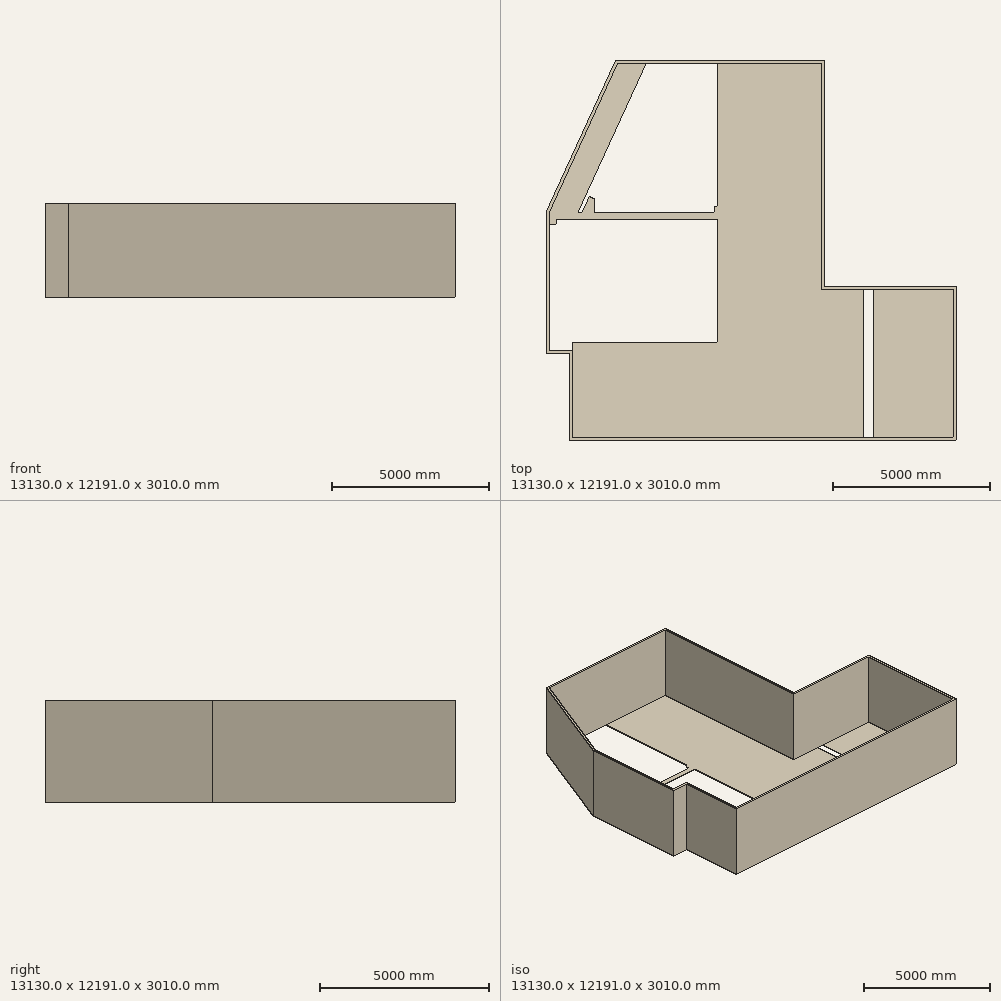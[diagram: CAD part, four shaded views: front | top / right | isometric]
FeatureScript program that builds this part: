
annotation { "Feature Type Name" : "Feature", "Feature Type Description" : "" }
export const myFeature = defineFeature(function(context is Context, id is Id, definition is map)
    precondition{}
    {
        {
            var Q0;
            Q0=qCreatedBy(makeId("Top.planeOp"),FACE);
            var sketch = newSketch(context, id + "F0", { "sketchPlane" : qUnion([Q0])});
            skLineSegment(sketch, "E0.bottom", {"start": v(0, 0) * mm, "end": v(20000, 0) * mm, "construction": true});
            skLineSegment(sketch, "E0.top", {"start": v(0, 22000) * mm, "end": v(20000, 22000) * mm, "construction": true});
            skLineSegment(sketch, "E0.left", {"start": v(0, 0) * mm, "end": v(0, 22000) * mm, "construction": true});
            skLineSegment(sketch, "E0.right", {"start": v(20000, 0) * mm, "end": v(20000, 22000) * mm, "construction": true});
            skLineSegment(sketch, "E1.bottom", {"start": v(0, 0) * mm, "end": v(400, 0) * mm, "construction": true});
            skLineSegment(sketch, "E1.top", {"start": v(0, 400) * mm, "end": v(400, 400) * mm, "construction": true});
            skLineSegment(sketch, "E1.left", {"start": v(0, 0) * mm, "end": v(0, 400) * mm, "construction": true});
            skLineSegment(sketch, "E1.right", {"start": v(400, 0) * mm, "end": v(400, 400) * mm, "construction": true});
            skPoint(sketch, "E2", {"position": v(400, 400) * mm});
            skLineSegment(sketch, "E3", {"start": v(400, -1815.56) * mm, "end": v(13100, -1815.56) * mm, "construction": true});
            skPoint(sketch, "E3.startSnap0", {"position": v(400, 200) * mm});
            skPoint(sketch, "E4", {"position": v(6750, -1815.56) * mm});
            skSolve(sketch);
        }
        {
            var Q0;
            Q0=qCreatedBy(makeId("Top.planeOp"),FACE);
            var sketch = newSketch(context, id + "F1", { "sketchPlane" : qUnion([Q0])});
            skLineSegment(sketch, "E5.bottom", {"start": v(400, 400) * mm, "end": v(5050, 400) * mm});
            skLineSegment(sketch, "E5.top", {"start": v(400, 3200) * mm, "end": v(5050, 3200) * mm});
            skLineSegment(sketch, "E5.left", {"start": v(400, 400) * mm, "end": v(400, 3200) * mm});
            skLineSegment(sketch, "E5.right", {"start": v(5050, 400) * mm, "end": v(5050, 3200) * mm});
            skLineSegment(sketch, "E6.bottom", {"start": v(-330, 3440.5) * mm, "end": v(5050, 3440.5) * mm});
            skLineSegment(sketch, "E6.top", {"start": v(-330, 7380.5) * mm, "end": v(5050, 7380.5) * mm});
            skLineSegment(sketch, "E6.left", {"start": v(-330, 3440.5) * mm, "end": v(-330, 7380.5) * mm});
            skLineSegment(sketch, "E6.right", {"start": v(5050, 3440.5) * mm, "end": v(5050, 7380.5) * mm});
            skLineSegment(sketch, "E7.bottom", {"start": v(8384.88, 7120) * mm, "end": v(6584.88, 7120) * mm});
            skLineSegment(sketch, "E7.top", {"start": v(8384.88, 4070) * mm, "end": v(6584.88, 4070) * mm});
            skLineSegment(sketch, "E7.left", {"start": v(8384.88, 7120) * mm, "end": v(8384.88, 4070) * mm});
            skLineSegment(sketch, "E7.right", {"start": v(6584.88, 7120) * mm, "end": v(6584.88, 4070) * mm});
            skLineSegment(sketch, "E8.bottom", {"start": v(12600, 5151.66) * mm, "end": v(10030, 5151.66) * mm});
            skLineSegment(sketch, "E8.top", {"start": v(12600, 400) * mm, "end": v(10030, 400) * mm});
            skLineSegment(sketch, "E8.left", {"start": v(12600, 5151.66) * mm, "end": v(12600, 400) * mm});
            skLineSegment(sketch, "E8.right", {"start": v(10030, 5151.66) * mm, "end": v(10030, 400) * mm});
            skLineSegment(sketch, "E9.bottom", {"start": v(5347.44, 7120) * mm, "end": v(6287.44, 7120) * mm});
            skLineSegment(sketch, "E9.top", {"start": v(5347.44, 400) * mm, "end": v(6287.44, 400) * mm});
            skLineSegment(sketch, "E9.left", {"start": v(5347.44, 7120) * mm, "end": v(5347.44, 400) * mm});
            skLineSegment(sketch, "E9.right", {"start": v(6287.44, 7120) * mm, "end": v(6287.44, 400) * mm});
            skLineSegment(sketch, "E10.bottom", {"start": v(6287.44, 400) * mm, "end": v(9732.56, 400) * mm});
            skLineSegment(sketch, "E10.top", {"start": v(6287.44, 2060) * mm, "end": v(9732.56, 2060) * mm});
            skLineSegment(sketch, "E10.left", {"start": v(6287.44, 400) * mm, "end": v(6287.44, 2060) * mm});
            skLineSegment(sketch, "E10.right", {"start": v(9732.56, 400) * mm, "end": v(9732.56, 2060) * mm});
            skLineSegment(sketch, "E11.bottom", {"start": v(8384.88, 2166.08) * mm, "end": v(6584.88, 2166.08) * mm});
            skLineSegment(sketch, "E11.top", {"start": v(8384.88, 4016.08) * mm, "end": v(6584.88, 4016.08) * mm});
            skLineSegment(sketch, "E11.left", {"start": v(8384.88, 2166.08) * mm, "end": v(8384.88, 4016.08) * mm});
            skLineSegment(sketch, "E11.right", {"start": v(6584.88, 2166.08) * mm, "end": v(6584.88, 4016.08) * mm});
            skLineSegment(sketch, "E12.bottom", {"start": v(9732.56, 2151.66) * mm, "end": v(8782.56, 2151.66) * mm});
            skLineSegment(sketch, "E12.top", {"start": v(9732.56, 5151.66) * mm, "end": v(8782.56, 5151.66) * mm});
            skLineSegment(sketch, "E12.left", {"start": v(9732.56, 2060) * mm, "end": v(9732.56, 5151.66) * mm});
            skLineSegment(sketch, "E12.right", {"start": v(8782.56, 2151.66) * mm, "end": v(8782.56, 5151.66) * mm});
            skLineSegment(sketch, "E13", {"start": v(-330, 7621.02) * mm, "end": v(1855.04, 12391.02) * mm});
            skLineSegment(sketch, "E14", {"start": v(1855.04, 12391.02) * mm, "end": v(5050, 12391.02) * mm});
            skLineSegment(sketch, "E15", {"start": v(5050, 12391.02) * mm, "end": v(5050, 7621.02) * mm});
            skLineSegment(sketch, "E16", {"start": v(5050, 7621.02) * mm, "end": v(-330, 7621.02) * mm});
            skLineSegment(sketch, "E17", {"start": v(587.33, 7621.02) * mm, "end": v(2772.37, 12391.02) * mm});
            skLineSegment(sketch, "E18.bottom", {"start": v(5347.44, 12391.02) * mm, "end": v(8384.88, 12391.02) * mm});
            skLineSegment(sketch, "E18.top", {"start": v(5347.44, 8631.02) * mm, "end": v(8384.88, 8631.02) * mm});
            skLineSegment(sketch, "E18.left", {"start": v(5347.44, 8631.02) * mm, "end": v(5347.44, 12391.02) * mm});
            skLineSegment(sketch, "E18.right", {"start": v(8384.88, 8631.02) * mm, "end": v(8384.88, 12391.02) * mm});
            skLineSegment(sketch, "E19", {"start": v(10030, 951.66) * mm, "end": v(12600, 951.66) * mm, "construction": true});
            skPoint(sketch, "E20", {"position": v(-330, 5410.5) * mm});
            skLineSegment(sketch, "E21", {"start": v(-6623.02, 7621.02) * mm, "end": v(-6623.02, 3200) * mm, "construction": true});
            skPoint(sketch, "E22", {"position": v(-6623.02, 5410.5) * mm});
            skPoint(sketch, "E23", {"position": v(5817.44, -1044.03) * mm});
            skPoint(sketch, "E24", {"position": v(5817.44, 400) * mm});
            skLineSegment(sketch, "E25.bottom", {"start": v(-110, 7380.5) * mm, "end": v(-330, 7380.5) * mm});
            skLineSegment(sketch, "E25.top", {"start": v(-110, 7240.5) * mm, "end": v(-330, 7240.5) * mm});
            skLineSegment(sketch, "E25.left", {"start": v(-110, 7380.5) * mm, "end": v(-110, 7240.5) * mm});
            skLineSegment(sketch, "E25.right", {"start": v(-330, 7380.5) * mm, "end": v(-330, 7240.5) * mm});
            skLineSegment(sketch, "E26", {"start": v(1120, 7621.02) * mm, "end": v(1120, 8039.5) * mm});
            skLineSegment(sketch, "E27", {"start": v(1120, 8039.5) * mm, "end": v(838.16, 8168.6) * mm});
            skLineSegment(sketch, "E28.bottom", {"start": v(5050, 7621.02) * mm, "end": v(4950, 7621.02) * mm});
            skLineSegment(sketch, "E28.top", {"start": v(5050, 7801.02) * mm, "end": v(4950, 7801.02) * mm});
            skLineSegment(sketch, "E28.left", {"start": v(5050, 7621.02) * mm, "end": v(5050, 7801.02) * mm});
            skLineSegment(sketch, "E28.right", {"start": v(4950, 7621.02) * mm, "end": v(4950, 7801.02) * mm});
            skLineSegment(sketch, "E29.bottom", {"start": v(12600, 5151.66) * mm, "end": v(12618.37, 5151.66) * mm});
            skLineSegment(sketch, "E29.top", {"start": v(12600, 4874.4) * mm, "end": v(12618.37, 4874.4) * mm});
            skLineSegment(sketch, "E29.left", {"start": v(12618.37, 5151.66) * mm, "end": v(12618.37, 4874.4) * mm});
            skLineSegment(sketch, "E29.right", {"start": v(12600, 5151.66) * mm, "end": v(12600, 4874.4) * mm});
            skLineSegment(sketch, "E30", {"start": v(717.56, 7621.02) * mm, "end": v(2902.6, 12391.02) * mm});
            skLineSegment(sketch, "E31", {"start": v(-330, 7621.02) * mm, "end": v(-330, 7380.5) * mm});
            skLineSegment(sketch, "E32", {"start": v(400, 3200) * mm, "end": v(400, 3440.5) * mm});
            skLineSegment(sketch, "E33", {"start": v(5050, 400) * mm, "end": v(5347.44, 400) * mm});
            skLineSegment(sketch, "E34", {"start": v(9732.56, 400) * mm, "end": v(10030, 400) * mm});
            skLineSegment(sketch, "E35", {"start": v(10030, 5151.66) * mm, "end": v(9732.56, 5151.66) * mm});
            skLineSegment(sketch, "E36", {"start": v(8782.56, 5151.66) * mm, "end": v(8384.88, 5151.66) * mm});
            skLineSegment(sketch, "E37", {"start": v(8384.88, 7120) * mm, "end": v(8384.88, 8631.02) * mm});
            skLineSegment(sketch, "E38", {"start": v(5050, 12391.02) * mm, "end": v(5347.44, 12391.02) * mm});
            skLineSegment(sketch, "E39", {"start": v(6584.88, 118.85) * mm, "end": v(5050, 118.85) * mm, "construction": true});
            skPoint(sketch, "E40", {"position": v(5817.44, 118.85) * mm});
            skLineSegment(sketch, "E41", {"start": v(5347.44, -349.5) * mm, "end": v(6287.44, -349.5) * mm, "construction": true});
            skPoint(sketch, "E42", {"position": v(5817.44, -349.5) * mm});
            skLineSegment(sketch, "E43", {"start": v(10030, -137.4) * mm, "end": v(8485.12, -137.4) * mm, "construction": true});
            skPoint(sketch, "E44", {"position": v(9257.56, 5151.66) * mm});
            skPoint(sketch, "E45", {"position": v(11591.26, 5335.33) * mm});
            skPoint(sketch, "E46", {"position": v(9257.56, -137.4) * mm});
            skPoint(sketch, "E47", {"position": v(9257.56, -547.39) * mm});
            skLineSegment(sketch, "E48", {"start": v(6287.44, -581.63) * mm, "end": v(6584.88, -581.63) * mm, "construction": true});
            skLineSegment(sketch, "E49", {"start": v(10030, -570.86) * mm, "end": v(9732.56, -570.86) * mm, "construction": true});
            skLineSegment(sketch, "E50", {"start": v(2902.6, 13575.57) * mm, "end": v(8384.88, 13575.57) * mm, "construction": true});
            skLineSegment(sketch, "E51", {"start": v(5050, 12932.31) * mm, "end": v(5347.44, 12932.31) * mm, "construction": true});
            skLineSegment(sketch, "E52", {"start": v(8802.5, 7120) * mm, "end": v(8802.5, 8631.02) * mm, "construction": true});
            skLineSegment(sketch, "E53", {"start": v(13053.8, 4070) * mm, "end": v(13053.8, 8631.02) * mm, "construction": true});
            skSolve(sketch);
        }
        {
            var Q0;
            Q0=qCreatedBy(makeId("Top.planeOp"),FACE);
            var sketch = newSketch(context, id + "F2", { "sketchPlane" : qUnion([Q0])});
            skPoint(sketch, "E54", {"position": v(400, 400) * mm});
            skPoint(sketch, "E55", {"position": v(-330, 3440.5) * mm});
            skPoint(sketch, "E56", {"position": v(-330, 7621.02) * mm});
            skPoint(sketch, "E57", {"position": v(1855.04, 12391.02) * mm});
            skPoint(sketch, "E58", {"position": v(8384.88, 12391.02) * mm});
            skPoint(sketch, "E59", {"position": v(8782.56, 5151.66) * mm});
            skPoint(sketch, "E60", {"position": v(12600, 5151.66) * mm});
            skPoint(sketch, "E61", {"position": v(12600, 400) * mm});
            skLineSegment(sketch, "E62", {"start": v(1855.04, 12391.02) * mm, "end": v(8384.88, 12391.02) * mm});
            skLineSegment(sketch, "E63", {"start": v(8384.88, 12391.02) * mm, "end": v(8384.88, 5151.66) * mm});
            skLineSegment(sketch, "E64", {"start": v(8384.88, 5151.66) * mm, "end": v(12600, 5151.66) * mm});
            skLineSegment(sketch, "E65", {"start": v(12600, 5151.66) * mm, "end": v(12600, 400) * mm});
            skLineSegment(sketch, "E66", {"start": v(12600, 400) * mm, "end": v(400, 400) * mm});
            skLineSegment(sketch, "E67", {"start": v(400, 400) * mm, "end": v(400, 3200) * mm});
            skLineSegment(sketch, "E68", {"start": v(400, 3200) * mm, "end": v(-330, 3200) * mm});
            skLineSegment(sketch, "E69", {"start": v(-330, 3200) * mm, "end": v(-330, 3440.5) * mm});
            skPoint(sketch, "E70", {"position": v(400, 3200) * mm});
            skLineSegment(sketch, "E71", {"start": v(-330, 3440.5) * mm, "end": v(-330, 7621.02) * mm});
            skLineSegment(sketch, "E72", {"start": v(1855.04, 12391.02) * mm, "end": v(-330, 7621.02) * mm});
            skLineSegment(sketch, "E73.0", {"start": v(1790.86, 12491.02) * mm, "end": v(-430, 7642.83) * mm});
            skLineSegment(sketch, "E73.1", {"start": v(-430, 3440.5) * mm, "end": v(-430, 7642.83) * mm});
            skLineSegment(sketch, "E73.2", {"start": v(1790.86, 12491.02) * mm, "end": v(8484.88, 12491.02) * mm});
            skLineSegment(sketch, "E73.3", {"start": v(-430, 3100) * mm, "end": v(-430, 3440.5) * mm});
            skLineSegment(sketch, "E73.4", {"start": v(300, 3100) * mm, "end": v(-430, 3100) * mm});
            skLineSegment(sketch, "E73.5", {"start": v(300, 300) * mm, "end": v(300, 3100) * mm});
            skLineSegment(sketch, "E73.6", {"start": v(8484.88, 12491.02) * mm, "end": v(8484.88, 5251.66) * mm});
            skLineSegment(sketch, "E73.7", {"start": v(8484.88, 5251.66) * mm, "end": v(12700, 5251.66) * mm});
            skLineSegment(sketch, "E73.8", {"start": v(12700, 5251.66) * mm, "end": v(12700, 300) * mm});
            skLineSegment(sketch, "E73.9", {"start": v(12700, 300) * mm, "end": v(300, 300) * mm});
            skSolve(sketch);
        }
        {
            var Q0;
            Q0=makeQuery(id+"F1.imprint","IMPRINT",FACE,{"disambiguationData":[TD([[makeQuery(id+"F1.imprint","IMPRINT",EDGE,{"derivedFrom":sQuery(id+"F1.wireOp",EDGE,"E5.bottom")}),1.0]])]});
            var Q1;
            Q1=makeQuery(id+"F1.imprint","IMPRINT",FACE,{"disambiguationData":[TD([[makeQuery(id+"F1.imprint","IMPRINT",EDGE,{"derivedFrom":sQuery(id+"F1.wireOp",EDGE,"E5.top")}),1.0]])]});
            var Q2;
            {var subQ6=sQuery(id+"F1.wireOp",EDGE,"E30");Q2=makeQuery(id+"F1.imprint","IMPRINT",FACE,{"disambiguationData":[TD([[makeQuery(id+"F1.imprint","IMPRINT",EDGE,{"derivedFrom":subQ6}),-1.0]])]});}
            var Q3;
            {var subQ3=sQuery(id+"F1.wireOp",EDGE,"E7.bottom");Q3=makeQuery(id+"F1.imprint","IMPRINT",FACE,{"disambiguationData":[TD([[makeQuery(id+"F1.imprint","IMPRINT",EDGE,{"derivedFrom":subQ3}),1.0]])]});}
            var Q4;
            {var subQ7=sQuery(id+"F1.wireOp",EDGE,"E15");Q4=makeQuery(id+"F1.imprint","IMPRINT",FACE,{"disambiguationData":[TD([[makeQuery(id+"F1.imprint","IMPRINT",EDGE,{"derivedFrom":subQ7}),-1.0]])]});}
            var Q5;
            Q5=makeQuery(id+"F1.imprint","IMPRINT",FACE,{"disambiguationData":[TD([[makeQuery(id+"F1.imprint","IMPRINT",EDGE,{"derivedFrom":sQuery(id+"F1.wireOp",EDGE,"E11.bottom")}),-1.0]])]});
            var Q6;
            Q6=makeQuery(id+"F1.imprint","IMPRINT",FACE,{"disambiguationData":[TD([[makeQuery(id+"F1.imprint","IMPRINT",EDGE,{"derivedFrom":sQuery(id+"F1.wireOp",EDGE,"E12.bottom")}),-1.0]])]});
            var Q7;
            Q7=makeQuery(id+"F1.imprint","IMPRINT",FACE,{"disambiguationData":[TD([[makeQuery(id+"F1.imprint","IMPRINT",EDGE,{"derivedFrom":sQuery(id+"F1.wireOp",EDGE,"E18.bottom")}),-1.0]])]});
            var Q8;
            Q8=makeQuery(id+"F1.imprint","IMPRINT",FACE,{"disambiguationData":[TD([[makeQuery(id+"F1.imprint","IMPRINT",EDGE,{"derivedFrom":sQuery(id+"F1.wireOp",EDGE,"E8.bottom")}),1.0]])]});
            var Q9;
            Q9=makeQuery(id+"F1.imprint","IMPRINT",FACE,{"disambiguationData":[TD([[makeQuery(id+"F1.imprint","IMPRINT",EDGE,{"derivedFrom":sQuery(id+"F1.wireOp",EDGE,"E6.top")}),-1.0]])]});
            var Q10;
            Q10=makeQuery(id+"F1.imprint","IMPRINT",FACE,{"disambiguationData":[TD([[makeQuery(id+"F1.imprint","IMPRINT",EDGE,{"derivedFrom":sQuery(id+"F1.wireOp",EDGE,"E10.bottom")}),1.0]])]});
            var Q11;
            Q11=makeQuery(id+"F1.imprint","IMPRINT",FACE,{"disambiguationData":[TD([[makeQuery(id+"F1.imprint","IMPRINT",EDGE,{"derivedFrom":sQuery(id+"F1.wireOp",EDGE,"E9.bottom")}),-1.0]])]});
            var Q12;
            {var subQ0=sQuery(id+"F1.wireOp",EDGE,"E13");Q12=makeQuery(id+"F1.imprint","IMPRINT",FACE,{"disambiguationData":[TD([[makeQuery(id+"F1.imprint","IMPRINT",EDGE,{"derivedFrom":subQ0}),-1.0]])]});}
            var Q13;
            {var subQ3=sQuery(id+"F1.wireOp",EDGE,"E26");Q13=makeQuery(id+"F1.imprint","IMPRINT",FACE,{"disambiguationData":[TD([[makeQuery(id+"F1.imprint","IMPRINT",EDGE,{"derivedFrom":subQ3}),1.0]])]});}
            var Q14;
            Q14=makeQuery(id+"F1.imprint","IMPRINT",FACE,{"disambiguationData":[TD([[makeQuery(id+"F1.imprint","IMPRINT",EDGE,{"derivedFrom":sQuery(id+"F1.wireOp",EDGE,"E25.bottom")}),1.0]])]});
            var Q15;
            Q15=makeQuery(id+"F1.imprint","IMPRINT",FACE,{"disambiguationData":[TD([[makeQuery(id+"F1.imprint","IMPRINT",EDGE,{"derivedFrom":sQuery(id+"F1.wireOp",EDGE,"E29.bottom")}),-1.0]])]});
            var Q16;
            Q16=makeQuery(id+"F1.imprint","IMPRINT",FACE,{"disambiguationData":[TD([[makeQuery(id+"F1.imprint","IMPRINT",EDGE,{"derivedFrom":sQuery(id+"F1.wireOp",EDGE,"E28.bottom")}),-1.0]])]});
            extrude(context, id + "F3", {"entities" : qUnion([Q0, Q1, Q2, Q3, Q4, Q5, Q6, Q7, Q8, Q9, Q10, Q11, Q12, Q13, Q14, Q15, Q16]), "oppositeDirection" : true, "depth" : 10 * mm});
        }
        {
            var Q0;
            Q0=makeQuery(id+"F2.imprint","IMPRINT",FACE,{"disambiguationData":[TD([[makeQuery(id+"F2.imprint","IMPRINT",EDGE,{"derivedFrom":sQuery(id+"F2.wireOp",EDGE,"E62")}),1.0]])]});
            extrude(context, id + "F4", {"entities" : qUnion([Q0]), "depth" : 3000 * mm, "hasSecondDirection" : true, "secondDirectionOppositeDirection" : true, "secondDirectionDepth" : 10 * mm});
        }
    });
